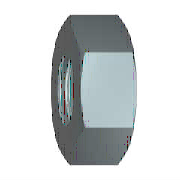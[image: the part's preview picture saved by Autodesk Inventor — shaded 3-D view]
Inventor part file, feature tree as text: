
AUTODESK INVENTOR PART (.ipt)
format: ipt  version: 2022 (Build 260153000, 153)  size: 173,568 bytes
history: native  units: mm (DEFAULTED — no unit token found)
features: sketch x3, other x2, extrude x1, hole x1, plane x1
ambient origin geometry x7: Origin, YZ Plane, XZ Plane, X Axis, Y Axis, Z Axis, Center Point
bodies: Solid1 (feature_tree)
feature tree (8):
  extrude  "Базовый элемент"  Depth=8.082904mm
  other  "Фаска1"
  hole  "Резьба"  [1 undecoded]
  other  "Work Axis1"
  plane  "Work Plane1"
  sketch  "Эскиз1"
  sketch  "Эскиз2"
  sketch  "Эскиз3"
note: 1 required parameter value undecoded (feature->parameter linkage not recoverable at this tier; creation-order binding heuristic only, values carry confidence <= 0.55)
